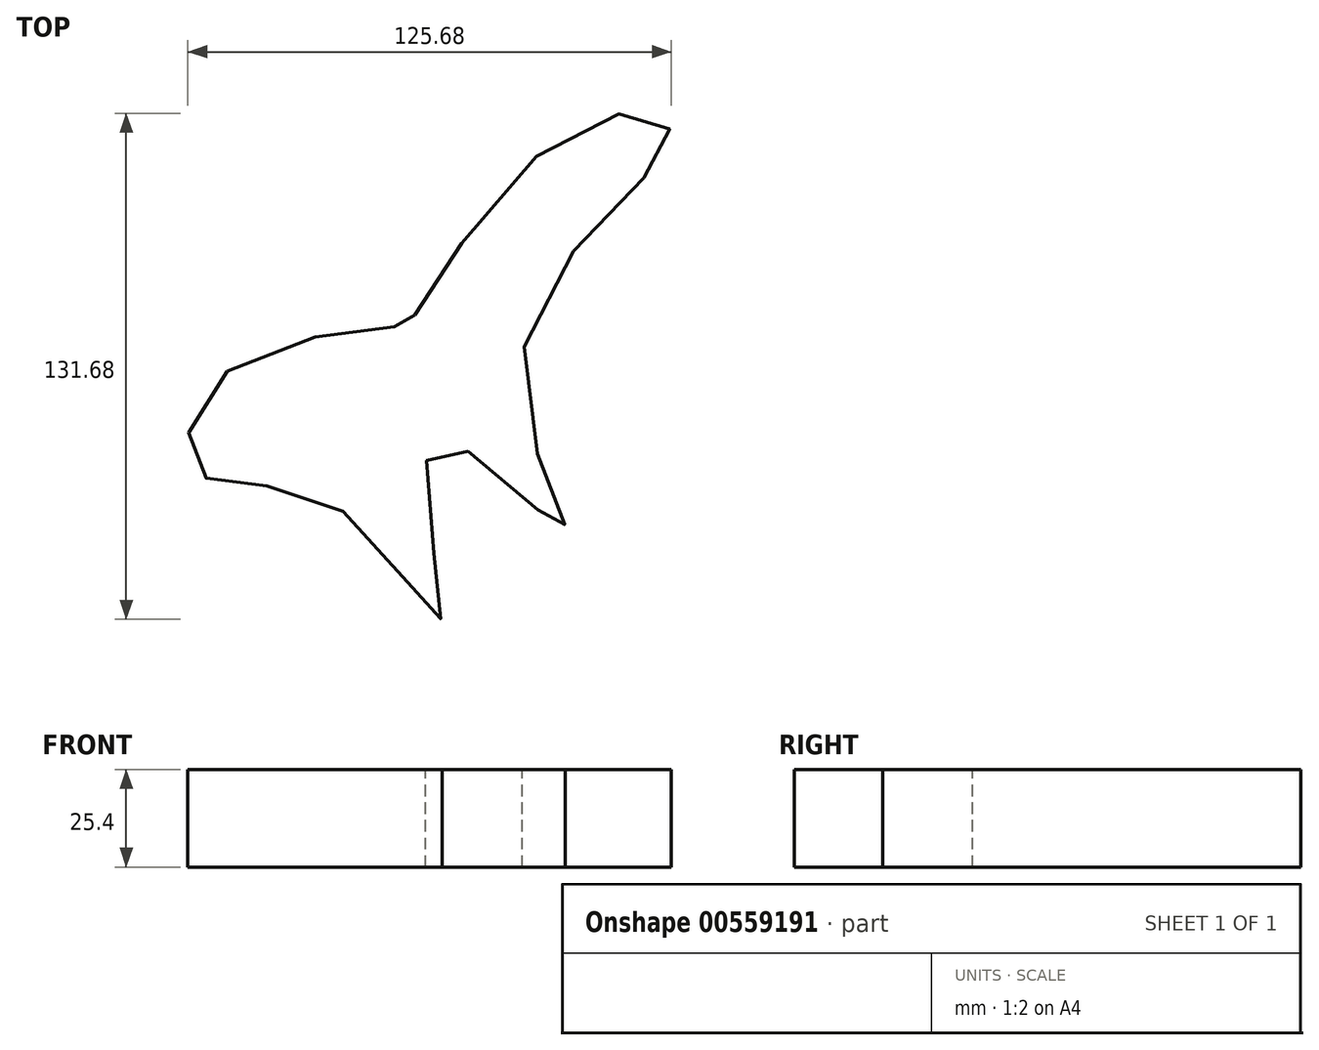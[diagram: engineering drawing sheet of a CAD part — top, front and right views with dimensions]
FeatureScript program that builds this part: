
annotation { "Feature Type Name" : "Feature", "Feature Type Description" : "" }
export const myFeature = defineFeature(function(context is Context, id is Id, definition is map)
    precondition{}
    {
        {
            var Q0;
            Q0=qCreatedBy(makeId("Top.planeOp"),FACE);
            var sketch = newSketch(context, id + "F0", { "sketchPlane" : qUnion([Q0])});
            skFitSpline(sketch, "E0", {"points": [v(-172.51, -169.52) * mm, v(-125.74, -157.8) * mm, v(-125.33, -157.57) * mm, v(-82.2, -106.45) * mm, v(-57.08, -108.33) * mm, v(-95.32, -163.19) * mm, v(-85.25, -210.9) * mm, v(-118.28, -188) * mm, v(-116.84, -233.54) * mm, v(-144.72, -204.37) * mm, v(-179.92, -196) * mm, v(-172.51, -169.52) * mm]});
            skSolve(sketch);
        }
        {
            var Q0;
            Q0=sQuery(id+"F0.wireOp",EDGE,"E0");
            extrude(context, id + "F1", {"bodyType" : ToolBodyType.SURFACE, "surfaceEntities" : qUnion([Q0]), "depth" : 25.4 * mm, "offsetDistance" : 25.4 * mm});
        }
    });
